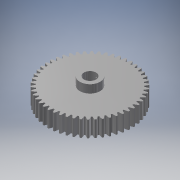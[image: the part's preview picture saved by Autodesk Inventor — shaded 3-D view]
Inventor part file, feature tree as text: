
AUTODESK INVENTOR PART (.ipt)
format: ipt  version: 2018 (Build 220112000, 112)  size: 367,104 bytes
history: native  units: mm (DEFAULTED — no unit token found)
features: sketch x5, plane x4, extrude x3, other x3, hole x1
ambient origin geometry x8: Origin, YZ Plane, XZ Plane, XY Plane, X Axis, Y Axis, Z Axis, Center Point
bodies: Solid1 (feature_tree)
feature tree (16):
  extrude  "Extrusion1"  Depth=20.0mm TaperAngle=0.0deg
  plane  "Work Plane2"
  plane  "Work Plane8"
  plane  "Work Plane9"
  other  "Engranaje recto"
  extrude  "Extrusión2"  Depth=10.0mm TaperAngle=0.0deg
  extrude  "Extrusión3"  Depth=0.628319mm TaperAngle=0.0deg
  plane  "Plano de trabajo11"
  hole  "Agujero2"  [1 undecoded]
  sketch  "Sketch1"  dims[d0=104.0mm d1=20.0mm d2=0.0mm]
  sketch  "Sketch2"  dims[d3=100.0mm d4=10.0mm d5=0.0mm]
  other  "Srf1"
  sketch  "Boceto3"  dims[d16=70.0mm d17=0.0mm d34=0.628319mm]
  sketch  "Boceto4"  dims[d39=0.0mm d41=0.0mm]
  sketch  "Boceto6"  dims[d43=70.0mm d46=70.0mm d47=0.0mm d48=0.0mm d49=25.0mm d50=10.0mm d51=0.0mm d52=15.0mm d53=30.0mm d54=0.0mm d63=5.0mm d64=3.0mm d65=1.425mm d66=3.708mm d67=3.023mm d68=2.0mm d69=14.3117mm d70=6.25mm d71=20.594885mm]
  other  "Diámetro de separación"
note: 1 required parameter value undecoded (feature->parameter linkage not recoverable at this tier; creation-order binding heuristic only, values carry confidence <= 0.55)
